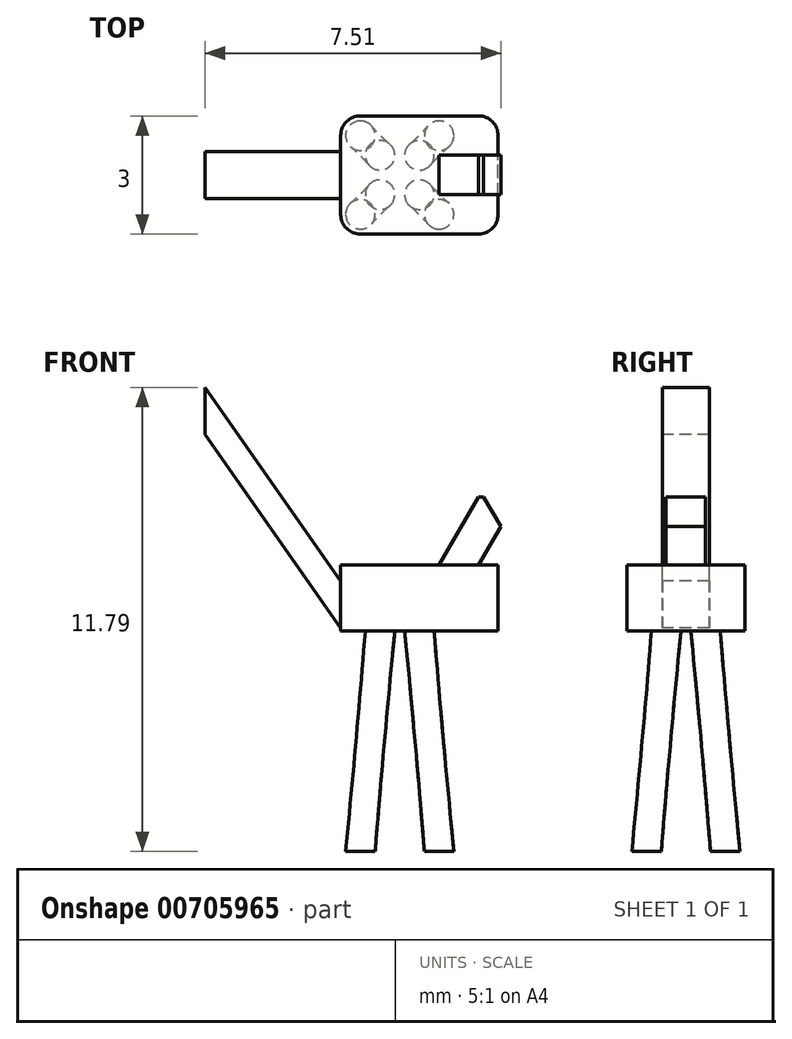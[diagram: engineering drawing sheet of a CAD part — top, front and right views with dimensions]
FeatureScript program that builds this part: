
annotation { "Feature Type Name" : "Feature", "Feature Type Description" : "" }
export const myFeature = defineFeature(function(context is Context, id is Id, definition is map)
    precondition{}
    {
        {
            var Q0;
            Q0=qCreatedBy(makeId("Top.planeOp"),FACE);
            var sketch = newSketch(context, id + "F0", { "sketchPlane" : qUnion([Q0])});
            skCircle(sketch, "E0", {"center": v(1, -1) * mm, "radius": 0.38 * mm});
            skLineSegment(sketch, "E1.bottom", {"start": v(1, -1) * mm, "end": v(-1, -1) * mm, "construction": true});
            skLineSegment(sketch, "E1.top", {"start": v(1, 1) * mm, "end": v(-1, 1) * mm, "construction": true});
            skLineSegment(sketch, "E1.left", {"start": v(1, -1) * mm, "end": v(1, 1) * mm, "construction": true});
            skLineSegment(sketch, "E1.right", {"start": v(-1, -1) * mm, "end": v(-1, 1) * mm, "construction": true});
            skCircle(sketch, "E2", {"center": v(-1, -1) * mm, "radius": 0.38 * mm});
            skCircle(sketch, "E3", {"center": v(-1, 1) * mm, "radius": 0.38 * mm});
            skCircle(sketch, "E4", {"center": v(1, 1) * mm, "radius": 0.38 * mm});
            skSolve(sketch);
        }
        {
            var Q0;
            Q0=qCreatedBy(makeId("Top.planeOp"),FACE);
            cPlane(context, id + "F1", {"entities" : qUnion([Q0]), "cplaneType" : CPlaneType.OFFSET, "offset" : (10 * .56) * mm, "width" : 150 * mm, "height" : 150 * mm});
        }
        {
            var Q0;
            Q0=qCreatedBy(makeId("Right.planeOp"),FACE);
            var sketch = newSketch(context, id + "F2", { "sketchPlane" : qUnion([Q0])});
            skLineSegment(sketch, "E5", {"start": v(0, 0) * mm, "end": v(0, 20.9) * mm, "construction": true});
            skSolve(sketch);
        }
        {
            var Q0;
            Q0=qCreatedBy(id+"F1.planeOp",FACE);
            var sketch = newSketch(context, id + "F3", { "sketchPlane" : qUnion([Q0])});
            skLineSegment(sketch, "E6.bottom", {"start": v(-0.5, 0.5) * mm, "end": v(0.5, 0.5) * mm, "construction": true});
            skLineSegment(sketch, "E6.top", {"start": v(-0.5, -0.5) * mm, "end": v(0.5, -0.5) * mm, "construction": true});
            skLineSegment(sketch, "E6.left", {"start": v(-0.5, 0.5) * mm, "end": v(-0.5, -0.5) * mm, "construction": true});
            skLineSegment(sketch, "E6.right", {"start": v(0.5, 0.5) * mm, "end": v(0.5, -0.5) * mm, "construction": true});
            skCircle(sketch, "E7", {"center": v(-0.5, 0.5) * mm, "radius": 0.38 * mm});
            skCircle(sketch, "E8", {"center": v(0.5, 0.5) * mm, "radius": 0.38 * mm});
            skCircle(sketch, "E9", {"center": v(-0.5, -0.5) * mm, "radius": 0.38 * mm});
            skCircle(sketch, "E10", {"center": v(0.5, -0.5) * mm, "radius": 0.38 * mm});
            skLineSegment(sketch, "E11.bottom", {"start": v(-1, 1) * mm, "end": v(1, 1) * mm});
            skLineSegment(sketch, "E11.top", {"start": v(-1, -1) * mm, "end": v(1, -1) * mm});
            skLineSegment(sketch, "E11.left", {"start": v(-1, 1) * mm, "end": v(-1, -1) * mm});
            skLineSegment(sketch, "E11.right", {"start": v(1, 1) * mm, "end": v(1, -1) * mm});
            skSolve(sketch);
        }
        {
            var Q0;
            Q0=makeQuery(id+"F0.imprint","IMPRINT",FACE,{"disambiguationData":[TD([[makeQuery(id+"F0.imprint","IMPRINT",EDGE,{"derivedFrom":sQuery(id+"F0.wireOp",EDGE,"E4")}),1.0]])]});
            var Q1;
            Q1=makeQuery(id+"F3.imprint","IMPRINT",FACE,{"disambiguationData":[TD([[makeQuery(id+"F3.imprint","IMPRINT",EDGE,{"derivedFrom":sQuery(id+"F3.wireOp",EDGE,"E8")}),1.0]])]});
            loft(context, id + "F4", {"sheetProfilesArray" : [{ "sheetProfileEntities" : qUnion([Q0]) }, { "sheetProfileEntities" : qUnion([Q1]) }]});
        }
        {
            var Q0;
            Q0=makeQuery(id+"F4.opLoft","SWEPT_BODY",BODY,{"disambiguationData":[OSD([makeQuery(id+"F0.imprint","IMPRINT",FACE,{"disambiguationData":[TD([[makeQuery(id+"F0.imprint","IMPRINT",EDGE,{"derivedFrom":sQuery(id+"F0.wireOp",EDGE,"E4")}),1.0]])]}),makeQuery(id+"F3.imprint","IMPRINT",FACE,{"disambiguationData":[TD([[makeQuery(id+"F3.imprint","IMPRINT",EDGE,{"derivedFrom":sQuery(id+"F3.wireOp",EDGE,"E8")}),1.0]])]})])]});
            var Q1;
            Q1=sQuery(id+"F2.wireOp",EDGE,"E5");
            circularPattern(context, id + "F5", {"entities" : qUnion([Q0]), "axis" : qUnion([Q1]), "angle" : 360 * degree, "instanceCount" : 4, "equalSpace" : true});
        }
        {
            var Q0;
            Q0=qCreatedBy(id+"F1.planeOp",FACE);
            var sketch = newSketch(context, id + "F6", { "sketchPlane" : qUnion([Q0])});
            skLineSegment(sketch, "E12.bottom", {"start": v(2, -1.5) * mm, "end": v(-1, -1.5) * mm});
            skLineSegment(sketch, "E12.top", {"start": v(2, 1.5) * mm, "end": v(-1, 1.5) * mm});
            skLineSegment(sketch, "E12.left", {"start": v(2.5, -1) * mm, "end": v(2.5, 1) * mm});
            skLineSegment(sketch, "E12.right", {"start": v(-1.5, -1) * mm, "end": v(-1.5, 1) * mm});
            skLineSegment(sketch, "E13", {"start": v(0, 0) * mm, "end": v(-1.5, 0) * mm, "construction": true});
            skLineSegment(sketch, "E14", {"start": v(0, 0) * mm, "end": v(0, -1.5) * mm, "construction": true});
            skPoint(sketch, "E15.visualSharp", {"position": v(-1.5, -1.5) * mm});
            skArc(sketch, "E15.filletArc", {"start": v(-1.5, -1) * mm, "mid": v(-1.35, -1.35) * mm, "end": v(-1, -1.5) * mm});
            skPoint(sketch, "E16.visualSharp", {"position": v(-1.5, 1.5) * mm});
            skArc(sketch, "E16.filletArc", {"start": v(-1, 1.5) * mm, "mid": v(-1.35, 1.35) * mm, "end": v(-1.5, 1) * mm});
            skPoint(sketch, "E17.visualSharp", {"position": v(2.5, 1.5) * mm});
            skArc(sketch, "E17.filletArc", {"start": v(2.5, 1) * mm, "mid": v(2.35, 1.35) * mm, "end": v(2, 1.5) * mm});
            skPoint(sketch, "E18.visualSharp", {"position": v(2.5, -1.5) * mm});
            skArc(sketch, "E18.filletArc", {"start": v(2, -1.5) * mm, "mid": v(2.35, -1.35) * mm, "end": v(2.5, -1) * mm});
            skSolve(sketch);
        }
        {
            var Q0;
            Q0 = qSketchRegion(id + "F6", true);
            var Q1;
            Q1=sQuery(id+"F6.wireOp",EDGE,"E12.right");
            var Q2;
            Q2=sQuery(id+"F6.wireOp",EDGE,"E12.left");
            var Q3;
            Q3=sQuery(id+"F6.wireOp",EDGE,"E12.top");
            var Q4;
            Q4=sQuery(id+"F6.wireOp",EDGE,"E12.bottom");
            extrude(context, id + "F7", {"entities" : qUnion([Q0]), "surfaceEntities" : qUnion([Q1, Q2, Q3, Q4]), "depth" : (3 * .56) * mm, "offsetDistance" : 25 * mm});
        }
        {
            var Q0;
            Q0=qCreatedBy(makeId("Front.planeOp"),FACE);
            var sketch = newSketch(context, id + "F8", { "sketchPlane" : qUnion([Q0])});
            skLineSegment(sketch, "E19", {"start": v(-1.5, 6.28) * mm, "end": v(-4.94, 11.2) * mm});
            skSolve(sketch);
        }
        {
            var Q0;
            Q0=makeQuery(id+"F7.opExtrude","SWEPT_FACE",FACE,{"disambiguationData":[OSD([sQuery(id+"F6.wireOp",EDGE,"E12.right")])]});
            var sketch = newSketch(context, id + "F9", { "sketchPlane" : qUnion([Q0])});
            skLineSegment(sketch, "E20.bottom", {"start": v(-0.6, 6.88) * mm, "end": v(0.6, 6.88) * mm});
            skLineSegment(sketch, "E20.top", {"start": v(-0.6, 5.68) * mm, "end": v(0.6, 5.68) * mm});
            skLineSegment(sketch, "E20.left", {"start": v(-0.6, 6.88) * mm, "end": v(-0.6, 5.68) * mm});
            skLineSegment(sketch, "E20.right", {"start": v(0.6, 6.88) * mm, "end": v(0.6, 5.68) * mm});
            skSolve(sketch);
        }
        {
            var Q0;
            Q0 = qSketchRegion(id + "F9", true);
            var Q1;
            Q1 = qConstructionFilter(qBodyType(qCreatedBy(id + "F8" ,EDGE), BodyType.WIRE), ConstructionObject.NO);
            sweep(context, id + "F10", {"operationType" : NewBodyOperationType.ADD, "profiles" : qUnion([Q0]), "path" : qUnion([Q1])});
        }
        {
            var Q0;
            Q0=makeQuery(id+"F7.opExtrude","CAP_FACE",FACE,{"disambiguationData":[OSD([sQuery(id+"F6.wireOp",EDGE,"E12.bottom"),sQuery(id+"F6.wireOp",EDGE,"E12.top"),sQuery(id+"F6.wireOp",EDGE,"E12.left"),sQuery(id+"F6.wireOp",EDGE,"E12.right"),sQuery(id+"F6.wireOp",EDGE,"E15.filletArc"),sQuery(id+"F6.wireOp",EDGE,"E16.filletArc"),sQuery(id+"F6.wireOp",EDGE,"E17.filletArc"),sQuery(id+"F6.wireOp",EDGE,"E18.filletArc")])],"isStart":false});
            var sketch = newSketch(context, id + "F11", { "sketchPlane" : qUnion([Q0])});
            skLineSegment(sketch, "E21.bottom", {"start": v(2, -0.5) * mm, "end": v(1, -0.5) * mm});
            skLineSegment(sketch, "E21.top", {"start": v(2, 0.5) * mm, "end": v(1, 0.5) * mm});
            skLineSegment(sketch, "E21.left", {"start": v(2, -0.5) * mm, "end": v(2, 0.5) * mm});
            skLineSegment(sketch, "E21.right", {"start": v(1, -0.5) * mm, "end": v(1, 0.5) * mm});
            skSolve(sketch);
        }
        {
            var Q0;
            Q0=qCreatedBy(makeId("Front.planeOp"),FACE);
            var sketch = newSketch(context, id + "F12", { "sketchPlane" : qUnion([Q0])});
            skLineSegment(sketch, "E22", {"start": v(1.5, 7.32) * mm, "end": v(2.5, 9.05) * mm});
            skLineSegment(sketch, "E23", {"start": v(1.5, 7.32) * mm, "end": v(0, 7.32) * mm});
            skSolve(sketch);
        }
        {
            var Q0;
            Q0=makeQuery(id+"F11.imprint","IMPRINT",FACE,{"disambiguationData":[TD([[makeQuery(id+"F11.imprint","IMPRINT",EDGE,{"derivedFrom":sQuery(id+"F11.wireOp",EDGE,"E21.bottom")}),-1.0]])]});
            var Q1;
            Q1=sQuery(id+"F12.wireOp",EDGE,"E22");
            sweep(context, id + "F13", {"operationType" : NewBodyOperationType.ADD, "profiles" : qUnion([Q0]), "path" : qUnion([Q1])});
        }
        {
            var Q0;
            Q0=makeQuery(id+"F13.opSweep","CAP_EDGE",EDGE,{"disambiguationData":[OSD([sQuery(id+"F11.wireOp",EDGE,"E21.left"),sQuery(id+"F12.wireOp",VERTEX,"E22.end")])],"isStart":false});
            chamfer(context, id + "F14", {"entities" : qUnion([Q0]), "width" : .5 * mm, "tangentPropagation" : true});
        }
    });
